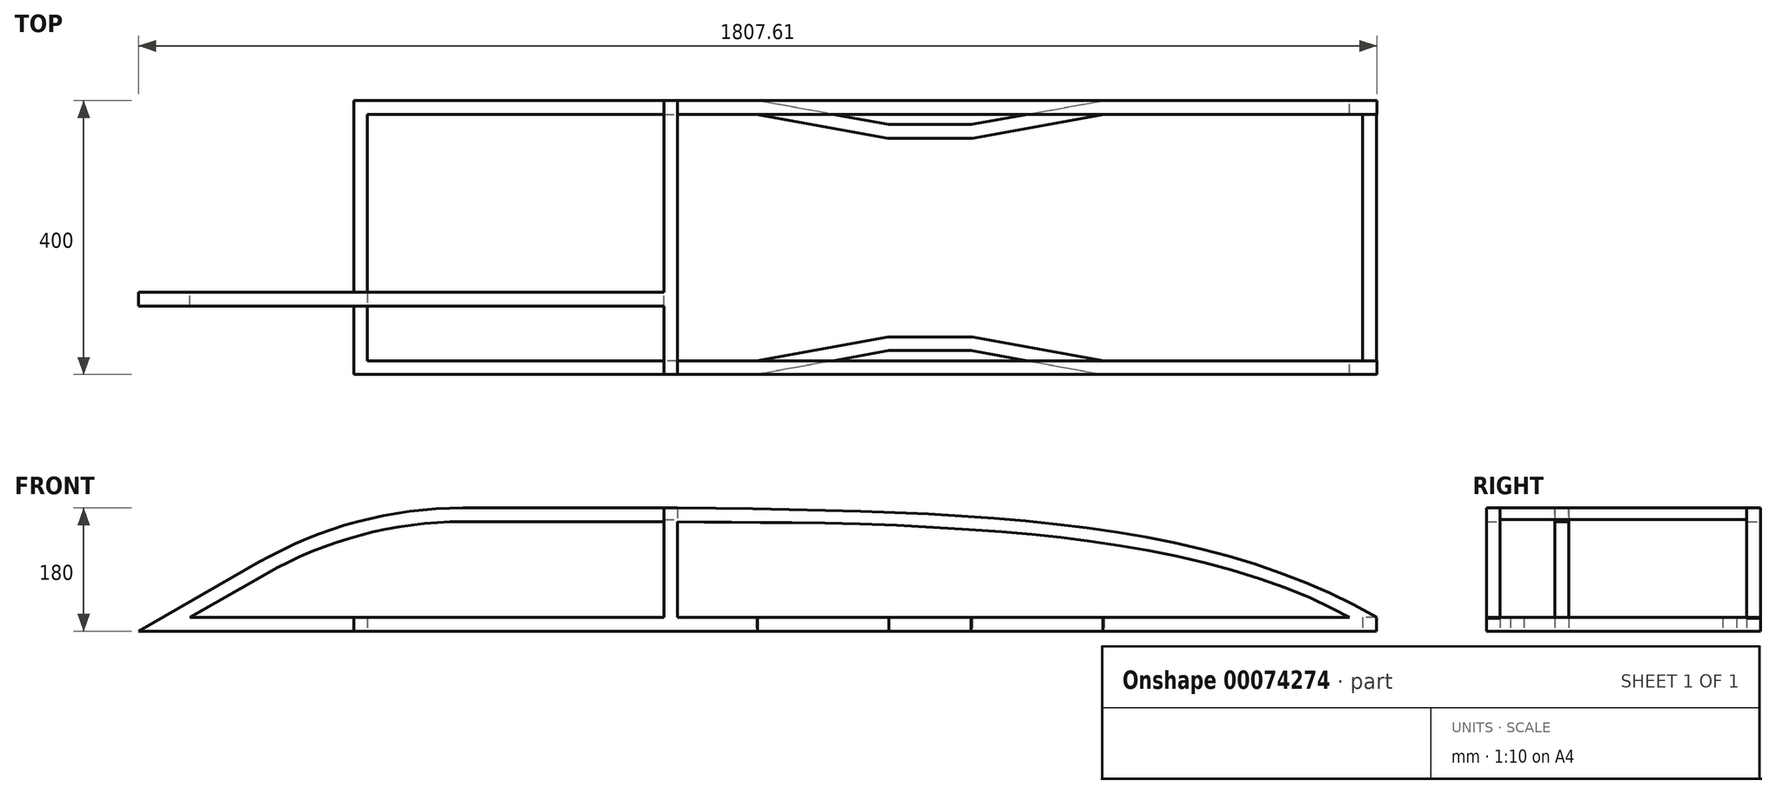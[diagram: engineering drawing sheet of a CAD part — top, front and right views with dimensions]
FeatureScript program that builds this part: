
annotation { "Feature Type Name" : "Feature", "Feature Type Description" : "" }
export const myFeature = defineFeature(function(context is Context, id is Id, definition is map)
    precondition{}
    {
        {
            var Q0;
            Q0=qCreatedBy(makeId("Top.planeOp"),FACE);
            var sketch = newSketch(context, id + "F0", { "sketchPlane" : qUnion([Q0])});
            skLineSegment(sketch, "E0.rect.bottom", {"start": v(-726.5, 180) * mm, "end": v(-158.61, 180) * mm});
            skLineSegment(sketch, "E0.rect.top", {"start": v(-726.5, -180) * mm, "end": v(-158.61, -180) * mm});
            skLineSegment(sketch, "E0.rect.left", {"start": v(-726.5, 180) * mm, "end": v(-726.5, -180) * mm});
            skLineSegment(sketch, "E0.rect.right", {"start": v(726.5, 180) * mm, "end": v(726.5, -180) * mm});
            skPoint(sketch, "E0.rect.middle", {"position": v(0, 0) * mm});
            skLineSegment(sketch, "E1.0", {"start": v(-746.5, 200) * mm, "end": v(-156.8, 200) * mm});
            skLineSegment(sketch, "E1.1", {"start": v(-746.5, 200) * mm, "end": v(-746.5, -200) * mm});
            skLineSegment(sketch, "E1.2", {"start": v(-746.5, -200) * mm, "end": v(-156.8, -200) * mm});
            skLineSegment(sketch, "E1.3", {"start": v(746.5, 200) * mm, "end": v(746.5, -200) * mm});
            skLineSegment(sketch, "E2", {"start": v(-293.5, 200) * mm, "end": v(-293.5, 180) * mm});
            skLineSegment(sketch, "E3", {"start": v(-293.5, -180) * mm, "end": v(-293.5, -200) * mm});
            skLineSegment(sketch, "E4", {"start": v(-273.5, 200) * mm, "end": v(-273.5, 180) * mm});
            skLineSegment(sketch, "E5", {"start": v(-273.5, -180) * mm, "end": v(-273.5, -200) * mm});
            skLineSegment(sketch, "E6", {"start": v(95.16, 165) * mm, "end": v(155.16, 165) * mm});
            skLineSegment(sketch, "E7.MirrorCS", {"start": v(95.16, 165) * mm, "end": v(35.16, 165) * mm});
            skLineSegment(sketch, "E8", {"start": v(155.16, 165) * mm, "end": v(347.12, 200) * mm});
            skLineSegment(sketch, "E9.0", {"start": v(156.97, 145) * mm, "end": v(350.71, 180.32) * mm});
            skLineSegment(sketch, "E9.1", {"start": v(95.16, 145) * mm, "end": v(156.97, 145) * mm});
            skLineSegment(sketch, "E10.MirrorCS", {"start": v(33.35, 145) * mm, "end": v(-160.4, 180.32) * mm});
            skLineSegment(sketch, "E11.MirrorCS", {"start": v(95.16, 145) * mm, "end": v(33.35, 145) * mm});
            skLineSegment(sketch, "E12.MirrorCS", {"start": v(35.16, 165) * mm, "end": v(-156.8, 200) * mm});
            skLineSegment(sketch, "E13.trimOffspring", {"start": v(348.93, 180) * mm, "end": v(726.5, 180) * mm});
            skLineSegment(sketch, "E14.trimOffspring", {"start": v(347.12, 200) * mm, "end": v(746.5, 200) * mm});
            skLineSegment(sketch, "E15", {"start": v(-746.5, 0) * mm, "end": v(338.63, 0) * mm, "construction": true});
            skLineSegment(sketch, "E16.MirrorCS", {"start": v(95.16, -145) * mm, "end": v(33.35, -145) * mm});
            skLineSegment(sketch, "E17.MirrorCS", {"start": v(95.16, -145) * mm, "end": v(156.97, -145) * mm});
            skLineSegment(sketch, "E18.MirrorCS", {"start": v(156.97, -145) * mm, "end": v(350.71, -180.32) * mm});
            skLineSegment(sketch, "E19.MirrorCS", {"start": v(155.16, -165) * mm, "end": v(347.12, -200) * mm});
            skLineSegment(sketch, "E20.MirrorCS", {"start": v(95.16, -165) * mm, "end": v(155.16, -165) * mm});
            skLineSegment(sketch, "E21.MirrorCS", {"start": v(95.16, -165) * mm, "end": v(35.16, -165) * mm});
            skLineSegment(sketch, "E22.MirrorCS", {"start": v(33.35, -145) * mm, "end": v(-160.4, -180.32) * mm});
            skLineSegment(sketch, "E23.MirrorCS", {"start": v(35.16, -165) * mm, "end": v(-156.8, -200) * mm});
            skLineSegment(sketch, "E24.trimOffspring", {"start": v(348.93, -180) * mm, "end": v(726.5, -180) * mm});
            skLineSegment(sketch, "E25.trimOffspring", {"start": v(347.12, -200) * mm, "end": v(746.5, -200) * mm});
            skSolve(sketch);
        }
        {
            var Q0;
            Q0 = qSketchRegion(id + "F0", true);
            extrude(context, id + "F1", {"entities" : qUnion([Q0]), "depth" : 20 * mm});
        }
        {
            var Q0;
            {var subQ0=sQuery(id+"F0.wireOp",EDGE,"E2");Q0=makeQuery(id+"F0.imprint","IMPRINT",FACE,{"disambiguationData":[TD([[makeQuery(id+"F0.imprint","IMPRINT",EDGE,{"derivedFrom":subQ0}),1.0]])]});}
            var Q1;
            {var subQ0=sQuery(id+"F0.wireOp",EDGE,"E3");Q1=makeQuery(id+"F0.imprint","IMPRINT",FACE,{"disambiguationData":[TD([[makeQuery(id+"F0.imprint","IMPRINT",EDGE,{"derivedFrom":subQ0}),1.0]])]});}
            extrude(context, id + "F2", {"entities" : qUnion([Q0, Q1]), "operationType" : NewBodyOperationType.ADD, "depth" : 180 * mm});
        }
        {
            var Q0;
            {var subQ0=sQuery(id+"F0.wireOp",EDGE,"E0.rect.bottom");Q0=makeQuery(id+"F2.boolean.opBoolean","MERGE",FACE,{"derivedFrom":[makeQuery(id+"F1.opExtrude","SWEPT_FACE",FACE,{"disambiguationData":[OSD([subQ0])]}),makeQuery(id+"F2.opExtrude","SWEPT_FACE",FACE,{"disambiguationData":[OSD([subQ0])]})]});}
            var sketch = newSketch(context, id + "F3", { "sketchPlane" : qUnion([Q0])});
            skLineSegment(sketch, "E26", {"start": v(-293.5, 163.06) * mm, "end": v(-273.5, 163.06) * mm});
            skSolve(sketch);
        }
        {
            var Q0;
            Q0 = qSketchRegion(id + "F3", true);
            var Q1;
            {var subQ0=sQuery(id+"F3.wireOp",EDGE,"E26");Q1=makeQuery(id+"F3.imprint","IMPRINT",FACE,{"disambiguationData":[TD([[makeQuery(id+"F3.imprint","IMPRINT",EDGE,{"derivedFrom":subQ0}),1.0]])]});}
            extrude(context, id + "F4", {"entities" : qUnion([Q0, Q1]), "operationType" : NewBodyOperationType.ADD, "endBound" : BoundingType.UP_TO_NEXT, "depth" : 354.3 * mm});
        }
        {
            var Q0;
            {var subQ0=sQuery(id+"F0.wireOp",EDGE,"E1.0");Q0=makeQuery(id+"F2.boolean.opBoolean","MERGE",FACE,{"derivedFrom":[makeQuery(id+"F1.opExtrude","SWEPT_FACE",FACE,{"disambiguationData":[OSD([subQ0])]}),makeQuery(id+"F2.opExtrude","SWEPT_FACE",FACE,{"disambiguationData":[OSD([subQ0])]})]});}
            var sketch = newSketch(context, id + "F5", { "sketchPlane" : qUnion([Q0])});
            skCircle(sketch, "E27", {"center": v(-96.09, 20) * mm, "radius": 257.5 * mm, "construction": true});
            skLineSegment(sketch, "E28", {"start": v(273.5, 157.55) * mm, "end": v(-517.43, 0) * mm, "construction": true});
            skCircle(sketch, "E29", {"center": v(-517.43, 0) * mm, "radius": 170 * mm, "construction": true});
            skLineSegment(sketch, "E30", {"start": v(273.5, 20) * mm, "end": v(-726.5, 20) * mm, "construction": true});
            skLineSegment(sketch, "E31", {"start": v(-726.5, 20) * mm, "end": v(-726.5, 187.22) * mm, "construction": true});
            skLineSegment(sketch, "E32", {"start": v(293.5, 180) * mm, "end": v(586.7, 180) * mm});
            skLineSegment(sketch, "E33", {"start": v(885.14, 100.51) * mm, "end": v(1060.44, 0) * mm});
            skLineSegment(sketch, "E34", {"start": v(1060.44, 0) * mm, "end": v(746.5, 0) * mm});
            skCircle(sketch, "E35", {"center": v(1060.44, 0) * mm, "radius": 257.5 * mm, "construction": true});
            skPoint(sketch, "E36.visualSharp", {"position": v(746.5, 180) * mm});
            skArc(sketch, "E36.filletArc", {"start": v(885.14, 100.51) * mm, "mid": v(741.12, 159.79) * mm, "end": v(586.7, 180) * mm});
            skLineSegment(sketch, "E37.0", {"start": v(985.35, 20) * mm, "end": v(746.5, 20) * mm});
            skLineSegment(sketch, "E37.1", {"start": v(875.19, 83.16) * mm, "end": v(985.35, 20) * mm});
            skArc(sketch, "E37.2", {"start": v(875.19, 83.16) * mm, "mid": v(735.97, 140.46) * mm, "end": v(586.7, 160) * mm});
            skLineSegment(sketch, "E37.3", {"start": v(293.5, 160) * mm, "end": v(586.7, 160) * mm});
            skFitSpline(sketch, "E38", {"points": [v(273.5, 180) * mm, v(-747.17, 20) * mm], "startDerivative": vector(-1287.7, -14.22) * mm, "endDerivative": vector(-766.19, -443.9) * mm});
            skFitSpline(sketch, "E39.0", {"points": [v(273.72, 160) * mm, v(166.44, 158.82) * mm, v(14.46, 156.8) * mm, v(-170.73, 147.2) * mm, v(-301, 134.96) * mm, v(-422.74, 116.12) * mm, v(-536.08, 89.16) * mm, v(-641.22, 52.56) * mm, v(-706, 20.73) * mm, v(-737.14, 2.7) * mm]});
            skLineSegment(sketch, "E40", {"start": v(-747.17, 20) * mm, "end": v(-737.14, 2.7) * mm});
            skSolve(sketch);
        }
        {
            var Q0;
            Q0 = qSketchRegion(id + "F5", true);
            var Q1;
            {var subQ1=sQuery(id+"F5.wireOp",EDGE,"E32");Q1=makeQuery(id+"F5.imprint","IMPRINT",FACE,{"disambiguationData":[TD([[makeQuery(id+"F5.imprint","IMPRINT",EDGE,{"derivedFrom":subQ1}),-1.0]])]});}
            extrude(context, id + "F6", {"entities" : qUnion([Q0, Q1]), "operationType" : NewBodyOperationType.ADD, "oppositeDirection" : true, "depth" : 300 * mm, "hasSecondDirection" : true, "secondDirectionOppositeDirection" : true, "secondDirectionDepth" : 280 * mm});
        }
        {
            var Q0;
            {var subQ0=sQuery(id+"F5.wireOp",EDGE,"E38");Q0=makeQuery(id+"F5.imprint","IMPRINT",FACE,{"disambiguationData":[TD([[makeQuery(id+"F5.imprint","IMPRINT",EDGE,{"derivedFrom":subQ0}),1.0]])]});}
            extrude(context, id + "F7", {"entities" : qUnion([Q0]), "operationType" : NewBodyOperationType.ADD, "oppositeDirection" : true, "depth" : 20 * mm});
        }
        {
            var Q0;
            {var subQ0=sQuery(id+"F5.wireOp",EDGE,"E38");Q0=makeQuery(id+"F5.imprint","IMPRINT",FACE,{"disambiguationData":[TD([[makeQuery(id+"F5.imprint","IMPRINT",EDGE,{"derivedFrom":subQ0}),1.0]])]});}
            extrude(context, id + "F8", {"entities" : qUnion([Q0]), "operationType" : NewBodyOperationType.ADD, "oppositeDirection" : true, "depth" : 400 * mm, "hasSecondDirection" : true, "secondDirectionOppositeDirection" : true, "secondDirectionDepth" : 380 * mm});
        }
    });
